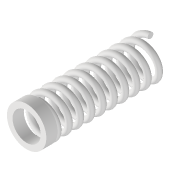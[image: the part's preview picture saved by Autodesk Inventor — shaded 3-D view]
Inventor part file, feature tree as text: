
AUTODESK INVENTOR PART (.ipt)
format: ipt  version: 2022 (Build 260153000, 153)  size: 326,144 bytes
history: native  units: mm
features: sketch x2, other x1, extrude x1
ambient origin geometry x8: Origin, YZ Plane, XZ Plane, XY Plane, X Axis, Y Axis, Z Axis, Center Point
bodies: Volumenkörper1 (feature_tree)
feature tree (4):
  other  "Spirale1"
  extrude  "Extrusion1"  Depth=1.5mm
  sketch  "Skizze1"  dims[d0=0.5mm d1=1.5mm]
  sketch  "Skizze2"  dims[d2=1.0mm d3=10.0mm d4=70.0mm d5=0.0mm d6=90.0deg d7=90.0deg d8=0.0mm d9=0.0mm d10=1.0mm d11=0.0mm]
